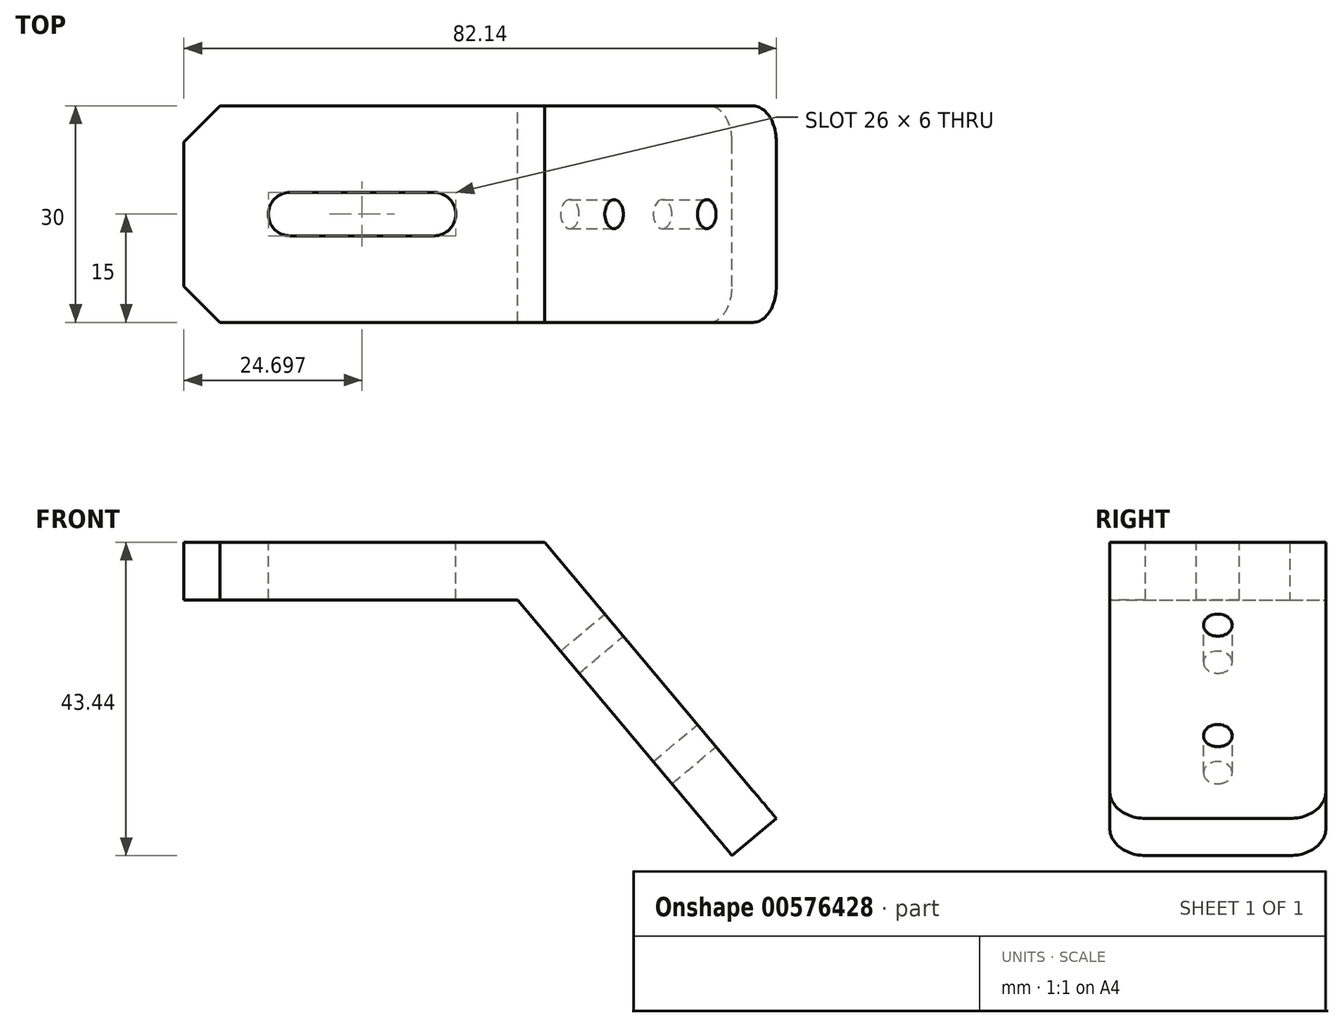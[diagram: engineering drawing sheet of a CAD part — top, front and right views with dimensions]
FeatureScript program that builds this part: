
annotation { "Feature Type Name" : "Feature", "Feature Type Description" : "" }
export const myFeature = defineFeature(function(context is Context, id is Id, definition is map)
    precondition{}
    {
        {
            var Q0;
            Q0=qCreatedBy(makeId("Front.planeOp"),FACE);
            var sketch = newSketch(context, id + "F0", { "sketchPlane" : qUnion([Q0])});
            skLineSegment(sketch, "E0", {"start": v(0, 0) * mm, "end": v(46.27, 0) * mm});
            skLineSegment(sketch, "E1", {"start": v(46.27, 0) * mm, "end": v(76.01, -35.44) * mm});
            skLineSegment(sketch, "E2.0", {"start": v(50, 8) * mm, "end": v(82.14, -30.3) * mm});
            skLineSegment(sketch, "E2.1", {"start": v(0, 8) * mm, "end": v(50, 8) * mm});
            skLineSegment(sketch, "E3", {"start": v(0, 0) * mm, "end": v(0, 8) * mm});
            skLineSegment(sketch, "E4", {"start": v(76.01, -35.44) * mm, "end": v(82.14, -30.3) * mm});
            skSolve(sketch);
        }
        {
            var Q0;
            Q0 = qSketchRegion(id + "F0", true);
            extrude(context, id + "F1", {"entities" : qUnion([Q0]), "endBound" : BoundingType.SYMMETRIC, "depth" : 30 * mm, "offsetDistance" : 25 * mm});
        }
        {
            var Q0;
            Q0=makeQuery(id+"F1.opExtrude","SWEPT_FACE",FACE,{"disambiguationData":[OSD([sQuery(id+"F0.wireOp",EDGE,"E2.1")])]});
            var sketch = newSketch(context, id + "F2", { "sketchPlane" : qUnion([Q0])});
            skLineSegment(sketch, "E5", {"start": v(14.7, 0) * mm, "end": v(34.7, 0) * mm});
            skArc(sketch, "E6.0.startCap", {"start": v(14.7, -3) * mm, "mid": v(11.7, 0) * mm, "end": v(14.7, 3) * mm});
            skArc(sketch, "E6.0.endCap", {"start": v(34.7, 3) * mm, "mid": v(37.7, 0) * mm, "end": v(34.7, -3) * mm});
            skLineSegment(sketch, "E6.0.left", {"start": v(14.7, 3) * mm, "end": v(34.7, 3) * mm});
            skLineSegment(sketch, "E6.0.right", {"start": v(14.7, -3) * mm, "end": v(34.7, -3) * mm});
            skSolve(sketch);
        }
        {
            var Q0;
            Q0 = qSketchRegion(id + "F2", true);
            extrude(context, id + "F3", {"entities" : qUnion([Q0]), "operationType" : NewBodyOperationType.REMOVE, "endBound" : BoundingType.THROUGH_ALL, "oppositeDirection" : true, "depth" : 25 * mm, "offsetDistance" : 25 * mm});
        }
        {
            var Q0;
            Q0=makeQuery(id+"F1.opExtrude","SWEPT_FACE",FACE,{"disambiguationData":[OSD([sQuery(id+"F0.wireOp",EDGE,"E2.0")])]});
            var sketch = newSketch(context, id + "F4", { "sketchPlane" : qUnion([Q0])});
            skPoint(sketch, "E7", {"position": v(0, -41.01) * mm});
            skPoint(sketch, "E8", {"position": v(0, -61.01) * mm});
            skSolve(sketch);
        }
        {
            var Q0;
            Q0=sQuery(id+"F4.wireOp",VERTEX,"E7");
            var Q1;
            Q1=sQuery(id+"F4.wireOp",VERTEX,"E8");
            var Q2;
            Q2=makeQuery(id+"F1.opExtrude","SWEPT_BODY",BODY,{"disambiguationData":[OSD([sQuery(id+"F0.wireOp",EDGE,"E0"),sQuery(id+"F0.wireOp",EDGE,"E1"),sQuery(id+"F0.wireOp",EDGE,"E2.0"),sQuery(id+"F0.wireOp",EDGE,"E2.1"),sQuery(id+"F0.wireOp",EDGE,"E3"),sQuery(id+"F0.wireOp",EDGE,"E4")])]});
            hole(context, id + "F5", {"style" : HoleStyle.SIMPLE, "endStyle" : HoleEndStyle.THROUGH, "holeDiameter" : 4 * mm, "majorDiameter" : 5 * mm, "isTappedThrough" : true, "tappedDepth" : 12 * mm, "tapClearance" : 3, "locations" : qUnion([Q0, Q1]), "scope" : qUnion([Q2])});
        }
        {
            var Q0;
            Q0=makeQuery(id+"F1.opExtrude","CAP_EDGE",EDGE,{"disambiguationData":[OSD([sQuery(id+"F0.wireOp",EDGE,"E4")])],"isStart":false});
            var Q1;
            Q1=makeQuery(id+"F1.opExtrude","CAP_EDGE",EDGE,{"disambiguationData":[OSD([sQuery(id+"F0.wireOp",EDGE,"E4")])],"isStart":true});
            fillet(context, id + "F6", {"entities" : qUnion([Q0, Q1]), "radius" : 5 * mm, "tangentPropagation" : true, "allowEdgeOverflow" : false});
        }
        {
            var Q0;
            Q0=makeQuery(id+"F1.opExtrude","CAP_EDGE",EDGE,{"disambiguationData":[OSD([sQuery(id+"F0.wireOp",EDGE,"E3")])],"isStart":false});
            var Q1;
            Q1=makeQuery(id+"F1.opExtrude","CAP_EDGE",EDGE,{"disambiguationData":[OSD([sQuery(id+"F0.wireOp",EDGE,"E3")])],"isStart":true});
            chamfer(context, id + "F7", {"entities" : qUnion([Q0, Q1]), "width" : 5 * mm, "tangentPropagation" : true});
        }
    });
